# Revit family: Slitz
name_source: partatom
category: Мебель
revit_build: Autodesk Revit 2017 (Build: 20160225_1515(x64)
units: mm (PartAtom-declared; Revit-internal decimal feet)

## family parameters
Всегда вертикально = Да
Заголовок OmniClass = General Furniture and Specialties
На основе рабочей плоскости = Нет
Номер OmniClass = 23.40.20.00
Общий = Нет
При загрузке вырезать с полостями = Нет
Точка расчета площади = Нет

## types (21) — shared parameters
Table Top = Skandiform Wood Birch veneer
Изготовитель = Skandiform AB
Ключевая пометка = XBE.1
Комментарии к типоразмеру = Created by Astacus AB
Описание = Table with top in birch,- oak veneer or white solid laminate (F2255). Chassis in chromium.

## per-type parameters (varying)
| type | Column Height | Column foot | Disc | Height | URL | Группа модели |
| LB-689 | 438 мм | Slitz-Column foot-Simple | Slitz-Skiva-rund105 : Slitz-Disc-rund105 | 450 мм | http://www.biminfo.se | LB-689 |
| LB-690 | 438 мм | Slitz-Column foot-Simple | Slitz-Disc-Square | 450 мм | http://www.biminfo.se | LB-690 |
| LB-688 | 438 мм | Slitz-Column foot-Double | Slitz-Disc-Oblong | 450 мм | http://www.biminfo.se | LB-688 |
| LB-693 | 438 мм | Slitz-Column foot-Simple | Slitz-Disc-rund65 | 450 мм | http://www.biminfo.se | LB-693 |
| LB-694 | 438 мм | Slitz-Column foot-Simple | Slitz-Disc-rund85 | 450 мм | http://www.biminfo.se | LB-624 |
| LB-630 | 588 мм | Slitz-Column foot-Simple | Slitz-Disc-Square | 600 мм | http://www.biminfo.se | LB-630 |
| LB-628 | 588 мм | Slitz-Column foot-Double | Slitz-Disc-Oblong | 600 мм | http://www.biminfo.se | LB-628 |
| LB-633 | 588 мм | Slitz-Column foot-Simple | Slitz-Disc-rund65 | 600 мм | http://www.biminfo.se | LB-633 |
| LB-634 | 588 мм | Slitz-Column foot-Simple | Slitz-Disc-rund85 | 600 мм | http://www.biminfo.se | LB-634 |
| HB-589 | 688 мм | Slitz-Column foot-Simple | Slitz-Skiva-rund105 : Slitz-Disc-rund105 | 700 мм | http://www.biminfo.se | HB-589 |
| HB-590 | 688 мм | Slitz-Column foot-Simple | Slitz-Disc-Square | 700 мм | http://www.biminfo.se | HB-590 |
| HB-588 | 688 мм | Slitz-Column foot-Double | Slitz-Disc-Oblong | 700 мм | http://file-system.ru | HB-588 |
| HB-593 | 688 мм | Slitz-Column foot-Simple | Slitz-Disc-rund65 | 700 мм | http://www.biminfo.se | HB-593 |
| HB-594 | 688 мм | Slitz-Column foot-Simple | Slitz-Disc-rund85 | 700 мм | http://www.biminfo.se | HB-594 |
| HB-990 | 888 мм | Slitz-Column foot-Simple | Slitz-Disc-Square | 900 мм | http://www.biminfo.se | HB-990 |
| HB-988 | 888 мм | Slitz-Column foot-Double | Slitz-Disc-Oblong | 900 мм | http://www.biminfo.se | HB-988 |
| HB-993 | 888 мм | Slitz-Column foot-Simple | Slitz-Disc-rund65 | 900 мм | http://www.biminfo.se | HB-993 |
| HB-994 | 888 мм | Slitz-Column foot-Simple | Slitz-Disc-rund85 | 900 мм | http://www.biminfo.se | HB-994 |
| HB-790 | 1088 мм | Slitz-Column foot-Simple | Slitz-Disc-Square | 1100 мм | http://www.biminfo.se | HB-790 |
| HB-788 | 1088 мм | Slitz-Column foot-Double | Slitz-Disc-Oblong | 1100 мм | http://www.biminfo.se | HB-788 |
| HB-793 | 1088 мм | Slitz-Column foot-Simple | Slitz-Disc-rund85 | 1100 мм | http://www.biminfo.se | HB-793 |

## geometry (parser evidence)
native form markers: Blend x13, Sweep x38
no freeform markers — native parametric forms only
